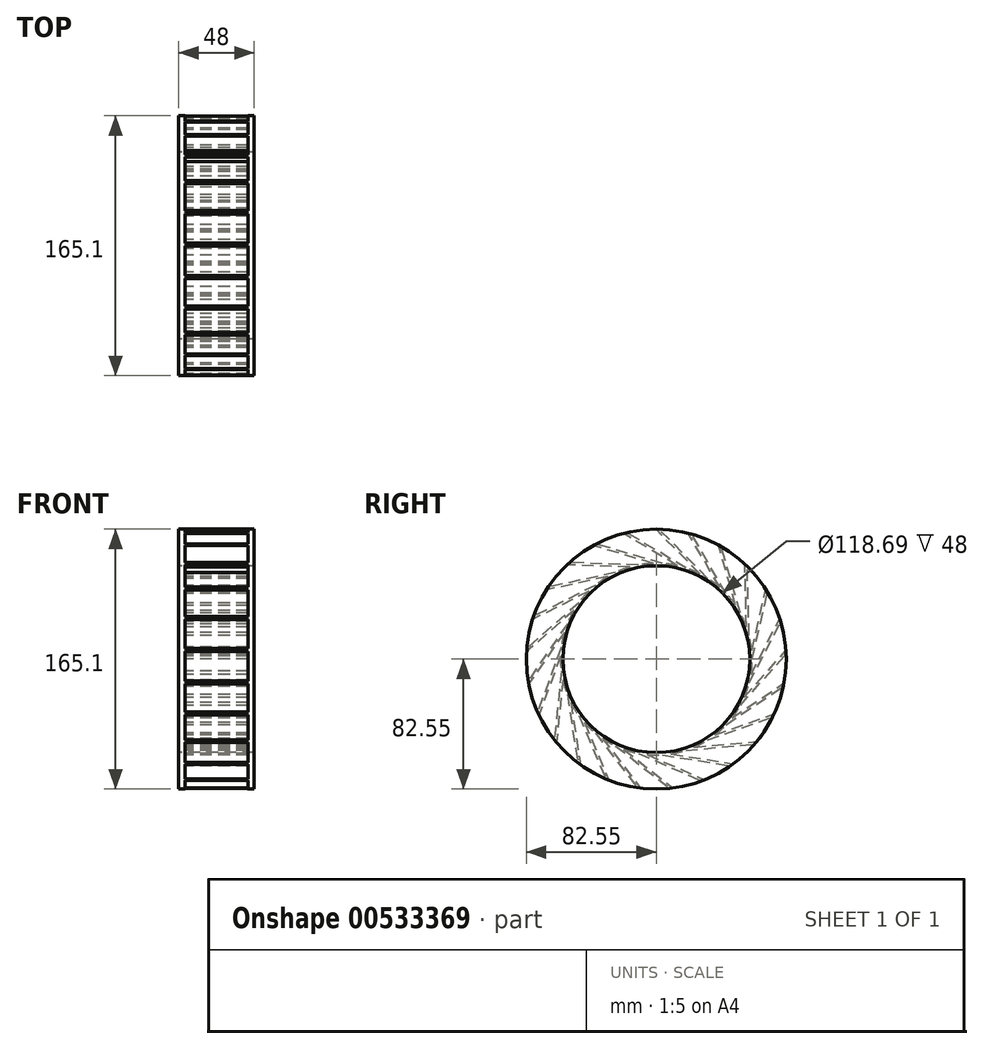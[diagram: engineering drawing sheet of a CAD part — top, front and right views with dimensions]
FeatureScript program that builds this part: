
annotation { "Feature Type Name" : "Feature", "Feature Type Description" : "" }
export const myFeature = defineFeature(function(context is Context, id is Id, definition is map)
    precondition{}
    {
        {
            var Q0;
            Q0=qCreatedBy(makeId("Right.planeOp"),FACE);
            var sketch = newSketch(context, id + "F0", { "sketchPlane" : qUnion([Q0])});
            skCircle(sketch, "E0", {"center": v(0, 0) * mm, "radius": 82.55 * mm});
            skCircle(sketch, "E1", {"center": v(0, 0) * mm, "radius": 60.85 * mm});
            skLineSegment(sketch, "E2", {"start": v(60.85, 0) * mm, "end": v(70.97, 44.2) * mm});
            skLineSegment(sketch, "E3.0", {"start": v(59.38, 0.34) * mm, "end": v(69.5, 44.53) * mm});
            skLineSegment(sketch, "E4", {"start": v(69.5, 44.53) * mm, "end": v(70.97, 44.2) * mm});
            skLineSegment(sketch, "E5.1.0", {"start": v(57.43, 15.1) * mm, "end": v(56.25, 60.42) * mm});
            skLineSegment(sketch, "E5.1.1", {"start": v(58.93, 15.13) * mm, "end": v(57.75, 60.46) * mm});
            skLineSegment(sketch, "E5.2.0", {"start": v(51.88, 28.9) * mm, "end": v(39.46, 72.5) * mm});
            skLineSegment(sketch, "E5.2.1", {"start": v(53.32, 29.31) * mm, "end": v(40.9, 72.92) * mm});
            skLineSegment(sketch, "E5.3.0", {"start": v(43.06, 40.9) * mm, "end": v(20.19, 80.04) * mm});
            skLineSegment(sketch, "E5.3.1", {"start": v(44.35, 41.65) * mm, "end": v(21.48, 80.8) * mm});
            skLineSegment(sketch, "E5.4.0", {"start": v(31.54, 50.32) * mm, "end": v(-0.35, 82.55) * mm});
            skLineSegment(sketch, "E5.4.1", {"start": v(32.6, 51.37) * mm, "end": v(0.71, 83.6) * mm});
            skLineSegment(sketch, "E5.5.0", {"start": v(18.03, 56.58) * mm, "end": v(-20.87, 79.87) * mm});
            skLineSegment(sketch, "E5.5.1", {"start": v(18.8, 57.87) * mm, "end": v(-20.1, 81.15) * mm});
            skLineSegment(sketch, "E5.6.0", {"start": v(3.4, 59.29) * mm, "end": v(-40.08, 72.17) * mm});
            skLineSegment(sketch, "E5.6.1", {"start": v(3.82, 60.73) * mm, "end": v(-39.65, 73.6) * mm});
            skLineSegment(sketch, "E5.7.0", {"start": v(-11.46, 58.27) * mm, "end": v(-56.77, 59.93) * mm});
            skLineSegment(sketch, "E5.7.1", {"start": v(-11.4, 59.77) * mm, "end": v(-56.71, 61.43) * mm});
            skLineSegment(sketch, "E5.8.0", {"start": v(-25.59, 53.59) * mm, "end": v(-69.89, 43.93) * mm});
            skLineSegment(sketch, "E5.8.1", {"start": v(-25.9, 55.05) * mm, "end": v(-70.2, 45.4) * mm});
            skLineSegment(sketch, "E5.9.0", {"start": v(-38.11, 45.54) * mm, "end": v(-78.62, 25.17) * mm});
            skLineSegment(sketch, "E5.9.1", {"start": v(-38.78, 46.88) * mm, "end": v(-79.3, 26.51) * mm});
            skLineSegment(sketch, "E5.10.0", {"start": v(-48.24, 34.63) * mm, "end": v(-82.4, 4.83) * mm});
            skLineSegment(sketch, "E5.10.1", {"start": v(-49.22, 35.76) * mm, "end": v(-83.4, 5.96) * mm});
            skLineSegment(sketch, "E5.11.0", {"start": v(-55.34, 21.55) * mm, "end": v(-81.02, -15.82) * mm});
            skLineSegment(sketch, "E5.11.1", {"start": v(-56.57, 22.4) * mm, "end": v(-82.26, -14.97) * mm});
            skLineSegment(sketch, "E5.12.0", {"start": v(-58.96, 7.11) * mm, "end": v(-74.54, -35.47) * mm});
            skLineSegment(sketch, "E5.12.1", {"start": v(-60.37, 7.63) * mm, "end": v(-75.95, -34.95) * mm});
            skLineSegment(sketch, "E5.13.0", {"start": v(-58.87, -7.78) * mm, "end": v(-63.38, -52.9) * mm});
            skLineSegment(sketch, "E5.13.1", {"start": v(-60.37, -7.63) * mm, "end": v(-64.87, -52.74) * mm});
            skLineSegment(sketch, "E5.14.0", {"start": v(-55.09, -22.17) * mm, "end": v(-48.24, -67) * mm});
            skLineSegment(sketch, "E5.14.1", {"start": v(-56.57, -22.4) * mm, "end": v(-49.72, -67.22) * mm});
            skLineSegment(sketch, "E5.15.0", {"start": v(-47.85, -35.18) * mm, "end": v(-30.06, -76.88) * mm});
            skLineSegment(sketch, "E5.15.1", {"start": v(-49.22, -35.76) * mm, "end": v(-31.44, -77.47) * mm});
            skLineSegment(sketch, "E5.16.0", {"start": v(-37.6, -45.97) * mm, "end": v(-10, -81.94) * mm});
            skLineSegment(sketch, "E5.16.1", {"start": v(-38.78, -46.88) * mm, "end": v(-11.19, -82.86) * mm});
            skLineSegment(sketch, "E5.17.0", {"start": v(-24.98, -53.87) * mm, "end": v(10.7, -81.85) * mm});
            skLineSegment(sketch, "E5.17.1", {"start": v(-25.9, -55.05) * mm, "end": v(9.77, -83.03) * mm});
            skLineSegment(sketch, "E5.18.0", {"start": v(-10.8, -58.4) * mm, "end": v(30.72, -76.62) * mm});
            skLineSegment(sketch, "E5.18.1", {"start": v(-11.4, -59.77) * mm, "end": v(30.11, -78) * mm});
            skLineSegment(sketch, "E5.19.0", {"start": v(4.06, -59.24) * mm, "end": v(48.8, -66.58) * mm});
            skLineSegment(sketch, "E5.19.1", {"start": v(3.82, -60.73) * mm, "end": v(48.56, -68.06) * mm});
            skLineSegment(sketch, "E5.20.0", {"start": v(18.67, -56.37) * mm, "end": v(63.83, -52.35) * mm});
            skLineSegment(sketch, "E5.20.1", {"start": v(18.8, -57.87) * mm, "end": v(63.96, -53.84) * mm});
            skLineSegment(sketch, "E5.21.0", {"start": v(32.1, -49.96) * mm, "end": v(74.84, -34.83) * mm});
            skLineSegment(sketch, "E5.21.1", {"start": v(32.6, -51.37) * mm, "end": v(75.34, -36.24) * mm});
            skLineSegment(sketch, "E5.22.0", {"start": v(43.52, -40.4) * mm, "end": v(81.15, -15.12) * mm});
            skLineSegment(sketch, "E5.22.1", {"start": v(44.35, -41.65) * mm, "end": v(81.99, -16.37) * mm});
            skLineSegment(sketch, "E5.23.0", {"start": v(52.2, -28.31) * mm, "end": v(82.36, 5.54) * mm});
            skLineSegment(sketch, "E5.23.1", {"start": v(53.32, -29.31) * mm, "end": v(83.48, 4.54) * mm});
            skLineSegment(sketch, "E5.24.0", {"start": v(57.6, -14.44) * mm, "end": v(78.4, 25.85) * mm});
            skLineSegment(sketch, "E5.24.1", {"start": v(58.93, -15.13) * mm, "end": v(79.73, 25.16) * mm});
            skLineSegment(sketch, "E6", {"start": v(-60.85, 0) * mm, "end": v(-59.35, 0) * mm});
            skCircle(sketch, "E7", {"center": v(0, 0) * mm, "radius": 59.35 * mm});
            skSolve(sketch);
        }
        {
            var Q0;
            {var subQ0=sQuery(id+"F0.wireOp",EDGE,"E5.22.0");var subQ1=sQuery(id+"F0.wireOp",EDGE,"E0");var subQ2=makeQuery(id+"F0.imprint","INTERSECT",VERTEX,{"derivedFrom":[subQ1,subQ0]});Q0=makeQuery(id+"F0.imprint","IMPRINT",FACE,{"disambiguationData":[TD([[makeQuery(id+"F0.imprint","IMPRINT",EDGE,{"disambiguationData":[TD([[subQ2,-1.0]])],"derivedFrom":subQ1}),1.0]])]});}
            var Q1;
            {var subQ0=sQuery(id+"F0.wireOp",EDGE,"E5.14.0");var subQ1=sQuery(id+"F0.wireOp",EDGE,"E0");var subQ2=makeQuery(id+"F0.imprint","INTERSECT",VERTEX,{"derivedFrom":[subQ1,subQ0]});Q1=makeQuery(id+"F0.imprint","IMPRINT",FACE,{"disambiguationData":[TD([[makeQuery(id+"F0.imprint","IMPRINT",EDGE,{"disambiguationData":[TD([[subQ2,-1.0]])],"derivedFrom":subQ1}),1.0]])]});}
            var Q2;
            {var subQ0=sQuery(id+"F0.wireOp",EDGE,"E5.6.0");var subQ1=sQuery(id+"F0.wireOp",EDGE,"E0");var subQ2=makeQuery(id+"F0.imprint","INTERSECT",VERTEX,{"derivedFrom":[subQ1,subQ0]});Q2=makeQuery(id+"F0.imprint","IMPRINT",FACE,{"disambiguationData":[TD([[makeQuery(id+"F0.imprint","IMPRINT",EDGE,{"disambiguationData":[TD([[subQ2,-1.0]])],"derivedFrom":subQ1}),1.0]])]});}
            var Q3;
            {var subQ0=sQuery(id+"F0.wireOp",EDGE,"E5.9.0");var subQ1=sQuery(id+"F0.wireOp",EDGE,"E0");var subQ2=makeQuery(id+"F0.imprint","INTERSECT",VERTEX,{"derivedFrom":[subQ1,subQ0]});Q3=makeQuery(id+"F0.imprint","IMPRINT",FACE,{"disambiguationData":[TD([[makeQuery(id+"F0.imprint","IMPRINT",EDGE,{"disambiguationData":[TD([[subQ2,-1.0]])],"derivedFrom":subQ1}),1.0]])]});}
            var Q4;
            {var subQ0=sQuery(id+"F0.wireOp",EDGE,"E5.3.0");var subQ1=sQuery(id+"F0.wireOp",EDGE,"E0");var subQ2=makeQuery(id+"F0.imprint","INTERSECT",VERTEX,{"derivedFrom":[subQ1,subQ0]});Q4=makeQuery(id+"F0.imprint","IMPRINT",FACE,{"disambiguationData":[TD([[makeQuery(id+"F0.imprint","IMPRINT",EDGE,{"disambiguationData":[TD([[subQ2,-1.0]])],"derivedFrom":subQ1}),1.0]])]});}
            var Q5;
            {var subQ0=sQuery(id+"F0.wireOp",EDGE,"E5.2.0");var subQ1=sQuery(id+"F0.wireOp",EDGE,"E0");var subQ2=makeQuery(id+"F0.imprint","INTERSECT",VERTEX,{"derivedFrom":[subQ1,subQ0]});Q5=makeQuery(id+"F0.imprint","IMPRINT",FACE,{"disambiguationData":[TD([[makeQuery(id+"F0.imprint","IMPRINT",EDGE,{"disambiguationData":[TD([[subQ2,-1.0]])],"derivedFrom":subQ1}),1.0]])]});}
            var Q6;
            {var subQ0=sQuery(id+"F0.wireOp",EDGE,"E5.1.0");var subQ1=sQuery(id+"F0.wireOp",EDGE,"E0");var subQ2=makeQuery(id+"F0.imprint","INTERSECT",VERTEX,{"derivedFrom":[subQ1,subQ0]});Q6=makeQuery(id+"F0.imprint","IMPRINT",FACE,{"disambiguationData":[TD([[makeQuery(id+"F0.imprint","IMPRINT",EDGE,{"disambiguationData":[TD([[subQ2,-1.0]])],"derivedFrom":subQ1}),1.0]])]});}
            var Q7;
            {var subQ3=sQuery(id+"F0.wireOp",EDGE,"E5.1.1");var subQ5=sQuery(id+"F0.wireOp",EDGE,"E1");var subQ6=makeQuery(id+"F0.imprint","INTERSECT",VERTEX,{"derivedFrom":[subQ5,subQ3]});Q7=makeQuery(id+"F0.imprint","IMPRINT",FACE,{"disambiguationData":[TD([[makeQuery(id+"F0.imprint","IMPRINT",EDGE,{"disambiguationData":[TD([[subQ6,1.0]])],"derivedFrom":subQ5}),-1.0]])]});}
            var Q8;
            {var subQ0=sQuery(id+"F0.wireOp",EDGE,"E5.24.0");var subQ1=sQuery(id+"F0.wireOp",EDGE,"E0");var subQ2=makeQuery(id+"F0.imprint","INTERSECT",VERTEX,{"derivedFrom":[subQ1,subQ0]});Q8=makeQuery(id+"F0.imprint","IMPRINT",FACE,{"disambiguationData":[TD([[makeQuery(id+"F0.imprint","IMPRINT",EDGE,{"disambiguationData":[TD([[subQ2,-1.0]])],"derivedFrom":subQ1}),1.0]])]});}
            var Q9;
            {var subQ0=sQuery(id+"F0.wireOp",EDGE,"E5.21.0");var subQ1=sQuery(id+"F0.wireOp",EDGE,"E0");var subQ2=makeQuery(id+"F0.imprint","INTERSECT",VERTEX,{"derivedFrom":[subQ1,subQ0]});Q9=makeQuery(id+"F0.imprint","IMPRINT",FACE,{"disambiguationData":[TD([[makeQuery(id+"F0.imprint","IMPRINT",EDGE,{"disambiguationData":[TD([[subQ2,-1.0]])],"derivedFrom":subQ1}),1.0]])]});}
            var Q10;
            {var subQ0=sQuery(id+"F0.wireOp",EDGE,"E5.8.0");var subQ1=sQuery(id+"F0.wireOp",EDGE,"E0");var subQ2=makeQuery(id+"F0.imprint","INTERSECT",VERTEX,{"derivedFrom":[subQ1,subQ0]});Q10=makeQuery(id+"F0.imprint","IMPRINT",FACE,{"disambiguationData":[TD([[makeQuery(id+"F0.imprint","IMPRINT",EDGE,{"disambiguationData":[TD([[subQ2,-1.0]])],"derivedFrom":subQ1}),1.0]])]});}
            var Q11;
            {var subQ0=sQuery(id+"F0.wireOp",EDGE,"E5.16.0");var subQ1=sQuery(id+"F0.wireOp",EDGE,"E0");var subQ2=makeQuery(id+"F0.imprint","INTERSECT",VERTEX,{"derivedFrom":[subQ1,subQ0]});Q11=makeQuery(id+"F0.imprint","IMPRINT",FACE,{"disambiguationData":[TD([[makeQuery(id+"F0.imprint","IMPRINT",EDGE,{"disambiguationData":[TD([[subQ2,-1.0]])],"derivedFrom":subQ1}),1.0]])]});}
            var Q12;
            {var subQ0=sQuery(id+"F0.wireOp",EDGE,"E5.11.0");var subQ1=sQuery(id+"F0.wireOp",EDGE,"E0");var subQ2=makeQuery(id+"F0.imprint","INTERSECT",VERTEX,{"derivedFrom":[subQ1,subQ0]});Q12=makeQuery(id+"F0.imprint","IMPRINT",FACE,{"disambiguationData":[TD([[makeQuery(id+"F0.imprint","IMPRINT",EDGE,{"disambiguationData":[TD([[subQ2,-1.0]])],"derivedFrom":subQ1}),1.0]])]});}
            var Q13;
            {var subQ3=sQuery(id+"F0.wireOp",EDGE,"E1");var subQ7=makeQuery(id+"F0.imprint","IMPRINT",VERTEX,{"derivedFrom":subQ3});Q13=makeQuery(id+"F0.imprint","IMPRINT",FACE,{"disambiguationData":[TD([[makeQuery(id+"F0.imprint","IMPRINT",EDGE,{"disambiguationData":[TD([[subQ7,1.0]])],"derivedFrom":subQ3}),-1.0]])]});}
            var Q14;
            {var subQ0=sQuery(id+"F0.wireOp",EDGE,"E5.20.0");var subQ1=sQuery(id+"F0.wireOp",EDGE,"E0");var subQ2=makeQuery(id+"F0.imprint","INTERSECT",VERTEX,{"derivedFrom":[subQ1,subQ0]});Q14=makeQuery(id+"F0.imprint","IMPRINT",FACE,{"disambiguationData":[TD([[makeQuery(id+"F0.imprint","IMPRINT",EDGE,{"disambiguationData":[TD([[subQ2,-1.0]])],"derivedFrom":subQ1}),1.0]])]});}
            var Q15;
            {var subQ0=sQuery(id+"F0.wireOp",EDGE,"E5.15.0");var subQ1=sQuery(id+"F0.wireOp",EDGE,"E0");var subQ2=makeQuery(id+"F0.imprint","INTERSECT",VERTEX,{"derivedFrom":[subQ1,subQ0]});Q15=makeQuery(id+"F0.imprint","IMPRINT",FACE,{"disambiguationData":[TD([[makeQuery(id+"F0.imprint","IMPRINT",EDGE,{"disambiguationData":[TD([[subQ2,-1.0]])],"derivedFrom":subQ1}),1.0]])]});}
            var Q16;
            {var subQ0=sQuery(id+"F0.wireOp",EDGE,"E5.10.0");var subQ1=sQuery(id+"F0.wireOp",EDGE,"E0");var subQ2=makeQuery(id+"F0.imprint","INTERSECT",VERTEX,{"derivedFrom":[subQ1,subQ0]});Q16=makeQuery(id+"F0.imprint","IMPRINT",FACE,{"disambiguationData":[TD([[makeQuery(id+"F0.imprint","IMPRINT",EDGE,{"disambiguationData":[TD([[subQ2,-1.0]])],"derivedFrom":subQ1}),1.0]])]});}
            var Q17;
            {var subQ0=sQuery(id+"F0.wireOp",EDGE,"E5.18.0");var subQ1=sQuery(id+"F0.wireOp",EDGE,"E0");var subQ2=makeQuery(id+"F0.imprint","INTERSECT",VERTEX,{"derivedFrom":[subQ1,subQ0]});Q17=makeQuery(id+"F0.imprint","IMPRINT",FACE,{"disambiguationData":[TD([[makeQuery(id+"F0.imprint","IMPRINT",EDGE,{"disambiguationData":[TD([[subQ2,-1.0]])],"derivedFrom":subQ1}),1.0]])]});}
            var Q18;
            {var subQ0=sQuery(id+"F0.wireOp",EDGE,"E5.17.0");var subQ1=sQuery(id+"F0.wireOp",EDGE,"E0");var subQ2=makeQuery(id+"F0.imprint","INTERSECT",VERTEX,{"derivedFrom":[subQ1,subQ0]});Q18=makeQuery(id+"F0.imprint","IMPRINT",FACE,{"disambiguationData":[TD([[makeQuery(id+"F0.imprint","IMPRINT",EDGE,{"disambiguationData":[TD([[subQ2,-1.0]])],"derivedFrom":subQ1}),1.0]])]});}
            var Q19;
            {var subQ0=sQuery(id+"F0.wireOp",EDGE,"E5.14.0");var subQ1=sQuery(id+"F0.wireOp",EDGE,"E0");var subQ2=makeQuery(id+"F0.imprint","INTERSECT",VERTEX,{"derivedFrom":[subQ1,subQ0]});Q19=makeQuery(id+"F0.imprint","IMPRINT",FACE,{"disambiguationData":[TD([[makeQuery(id+"F0.imprint","IMPRINT",EDGE,{"disambiguationData":[TD([[subQ2,1.0]])],"derivedFrom":subQ1}),1.0]])]});}
            var Q20;
            {var subQ0=sQuery(id+"F0.wireOp",EDGE,"E5.22.0");var subQ1=sQuery(id+"F0.wireOp",EDGE,"E0");var subQ2=makeQuery(id+"F0.imprint","INTERSECT",VERTEX,{"derivedFrom":[subQ1,subQ0]});Q20=makeQuery(id+"F0.imprint","IMPRINT",FACE,{"disambiguationData":[TD([[makeQuery(id+"F0.imprint","IMPRINT",EDGE,{"disambiguationData":[TD([[subQ2,1.0]])],"derivedFrom":subQ1}),1.0]])]});}
            var Q21;
            {var subQ0=sQuery(id+"F0.wireOp",EDGE,"E5.9.0");var subQ1=sQuery(id+"F0.wireOp",EDGE,"E0");var subQ2=makeQuery(id+"F0.imprint","INTERSECT",VERTEX,{"derivedFrom":[subQ1,subQ0]});Q21=makeQuery(id+"F0.imprint","IMPRINT",FACE,{"disambiguationData":[TD([[makeQuery(id+"F0.imprint","IMPRINT",EDGE,{"disambiguationData":[TD([[subQ2,1.0]])],"derivedFrom":subQ1}),1.0]])]});}
            var Q22;
            {var subQ0=sQuery(id+"F0.wireOp",EDGE,"E5.17.0");var subQ1=sQuery(id+"F0.wireOp",EDGE,"E0");var subQ2=makeQuery(id+"F0.imprint","INTERSECT",VERTEX,{"derivedFrom":[subQ1,subQ0]});Q22=makeQuery(id+"F0.imprint","IMPRINT",FACE,{"disambiguationData":[TD([[makeQuery(id+"F0.imprint","IMPRINT",EDGE,{"disambiguationData":[TD([[subQ2,1.0]])],"derivedFrom":subQ1}),1.0]])]});}
            var Q23;
            {var subQ0=sQuery(id+"F0.wireOp",EDGE,"E5.3.0");var subQ1=sQuery(id+"F0.wireOp",EDGE,"E0");var subQ2=makeQuery(id+"F0.imprint","INTERSECT",VERTEX,{"derivedFrom":[subQ1,subQ0]});Q23=makeQuery(id+"F0.imprint","IMPRINT",FACE,{"disambiguationData":[TD([[makeQuery(id+"F0.imprint","IMPRINT",EDGE,{"disambiguationData":[TD([[subQ2,1.0]])],"derivedFrom":subQ1}),1.0]])]});}
            var Q24;
            {var subQ0=sQuery(id+"F0.wireOp",EDGE,"E5.2.0");var subQ1=sQuery(id+"F0.wireOp",EDGE,"E0");var subQ2=makeQuery(id+"F0.imprint","INTERSECT",VERTEX,{"derivedFrom":[subQ1,subQ0]});Q24=makeQuery(id+"F0.imprint","IMPRINT",FACE,{"disambiguationData":[TD([[makeQuery(id+"F0.imprint","IMPRINT",EDGE,{"disambiguationData":[TD([[subQ2,1.0]])],"derivedFrom":subQ1}),1.0]])]});}
            var Q25;
            {var subQ0=sQuery(id+"F0.wireOp",EDGE,"E5.1.0");var subQ1=sQuery(id+"F0.wireOp",EDGE,"E0");var subQ2=makeQuery(id+"F0.imprint","INTERSECT",VERTEX,{"derivedFrom":[subQ1,subQ0]});Q25=makeQuery(id+"F0.imprint","IMPRINT",FACE,{"disambiguationData":[TD([[makeQuery(id+"F0.imprint","IMPRINT",EDGE,{"disambiguationData":[TD([[subQ2,1.0]])],"derivedFrom":subQ1}),1.0]])]});}
            var Q26;
            {var subQ0=sQuery(id+"F0.wireOp",EDGE,"E5.23.0");var subQ1=sQuery(id+"F0.wireOp",EDGE,"E0");var subQ2=makeQuery(id+"F0.imprint","INTERSECT",VERTEX,{"derivedFrom":[subQ1,subQ0]});Q26=makeQuery(id+"F0.imprint","IMPRINT",FACE,{"disambiguationData":[TD([[makeQuery(id+"F0.imprint","IMPRINT",EDGE,{"disambiguationData":[TD([[subQ2,-1.0]])],"derivedFrom":subQ1}),1.0]])]});}
            var Q27;
            {var subQ0=sQuery(id+"F0.wireOp",EDGE,"E5.13.0");var subQ1=sQuery(id+"F0.wireOp",EDGE,"E0");var subQ2=makeQuery(id+"F0.imprint","INTERSECT",VERTEX,{"derivedFrom":[subQ1,subQ0]});Q27=makeQuery(id+"F0.imprint","IMPRINT",FACE,{"disambiguationData":[TD([[makeQuery(id+"F0.imprint","IMPRINT",EDGE,{"disambiguationData":[TD([[subQ2,-1.0]])],"derivedFrom":subQ1}),1.0]])]});}
            var Q28;
            {var subQ0=sQuery(id+"F0.wireOp",EDGE,"E5.5.0");var subQ1=sQuery(id+"F0.wireOp",EDGE,"E0");var subQ2=makeQuery(id+"F0.imprint","INTERSECT",VERTEX,{"derivedFrom":[subQ1,subQ0]});Q28=makeQuery(id+"F0.imprint","IMPRINT",FACE,{"disambiguationData":[TD([[makeQuery(id+"F0.imprint","IMPRINT",EDGE,{"disambiguationData":[TD([[subQ2,-1.0]])],"derivedFrom":subQ1}),1.0]])]});}
            var Q29;
            {var subQ0=sQuery(id+"F0.wireOp",EDGE,"E5.4.0");var subQ1=sQuery(id+"F0.wireOp",EDGE,"E0");var subQ2=makeQuery(id+"F0.imprint","INTERSECT",VERTEX,{"derivedFrom":[subQ1,subQ0]});Q29=makeQuery(id+"F0.imprint","IMPRINT",FACE,{"disambiguationData":[TD([[makeQuery(id+"F0.imprint","IMPRINT",EDGE,{"disambiguationData":[TD([[subQ2,-1.0]])],"derivedFrom":subQ1}),1.0]])]});}
            var Q30;
            {var subQ0=sQuery(id+"F0.wireOp",EDGE,"E5.4.0");var subQ1=sQuery(id+"F0.wireOp",EDGE,"E0");var subQ2=makeQuery(id+"F0.imprint","INTERSECT",VERTEX,{"derivedFrom":[subQ1,subQ0]});Q30=makeQuery(id+"F0.imprint","IMPRINT",FACE,{"disambiguationData":[TD([[makeQuery(id+"F0.imprint","IMPRINT",EDGE,{"disambiguationData":[TD([[subQ2,1.0]])],"derivedFrom":subQ1}),1.0]])]});}
            var Q31;
            {var subQ0=sQuery(id+"F0.wireOp",EDGE,"E5.5.0");var subQ1=sQuery(id+"F0.wireOp",EDGE,"E0");var subQ2=makeQuery(id+"F0.imprint","INTERSECT",VERTEX,{"derivedFrom":[subQ1,subQ0]});Q31=makeQuery(id+"F0.imprint","IMPRINT",FACE,{"disambiguationData":[TD([[makeQuery(id+"F0.imprint","IMPRINT",EDGE,{"disambiguationData":[TD([[subQ2,1.0]])],"derivedFrom":subQ1}),1.0]])]});}
            var Q32;
            {var subQ0=sQuery(id+"F0.wireOp",EDGE,"E5.19.0");var subQ1=sQuery(id+"F0.wireOp",EDGE,"E0");var subQ2=makeQuery(id+"F0.imprint","INTERSECT",VERTEX,{"derivedFrom":[subQ1,subQ0]});Q32=makeQuery(id+"F0.imprint","IMPRINT",FACE,{"disambiguationData":[TD([[makeQuery(id+"F0.imprint","IMPRINT",EDGE,{"disambiguationData":[TD([[subQ2,-1.0]])],"derivedFrom":subQ1}),1.0]])]});}
            var Q33;
            {var subQ0=sQuery(id+"F0.wireOp",EDGE,"E5.8.0");var subQ1=sQuery(id+"F0.wireOp",EDGE,"E0");var subQ2=makeQuery(id+"F0.imprint","INTERSECT",VERTEX,{"derivedFrom":[subQ1,subQ0]});Q33=makeQuery(id+"F0.imprint","IMPRINT",FACE,{"disambiguationData":[TD([[makeQuery(id+"F0.imprint","IMPRINT",EDGE,{"disambiguationData":[TD([[subQ2,1.0]])],"derivedFrom":subQ1}),1.0]])]});}
            var Q34;
            {var subQ0=sQuery(id+"F0.wireOp",EDGE,"E5.11.0");var subQ1=sQuery(id+"F0.wireOp",EDGE,"E0");var subQ2=makeQuery(id+"F0.imprint","INTERSECT",VERTEX,{"derivedFrom":[subQ1,subQ0]});Q34=makeQuery(id+"F0.imprint","IMPRINT",FACE,{"disambiguationData":[TD([[makeQuery(id+"F0.imprint","IMPRINT",EDGE,{"disambiguationData":[TD([[subQ2,1.0]])],"derivedFrom":subQ1}),1.0]])]});}
            var Q35;
            {var subQ0=sQuery(id+"F0.wireOp",EDGE,"E5.19.0");var subQ1=sQuery(id+"F0.wireOp",EDGE,"E0");var subQ2=makeQuery(id+"F0.imprint","INTERSECT",VERTEX,{"derivedFrom":[subQ1,subQ0]});Q35=makeQuery(id+"F0.imprint","IMPRINT",FACE,{"disambiguationData":[TD([[makeQuery(id+"F0.imprint","IMPRINT",EDGE,{"disambiguationData":[TD([[subQ2,1.0]])],"derivedFrom":subQ1}),1.0]])]});}
            var Q36;
            {var subQ0=sQuery(id+"F0.wireOp",EDGE,"E5.12.0");var subQ1=sQuery(id+"F0.wireOp",EDGE,"E0");var subQ2=makeQuery(id+"F0.imprint","INTERSECT",VERTEX,{"derivedFrom":[subQ1,subQ0]});Q36=makeQuery(id+"F0.imprint","IMPRINT",FACE,{"disambiguationData":[TD([[makeQuery(id+"F0.imprint","IMPRINT",EDGE,{"disambiguationData":[TD([[subQ2,1.0]])],"derivedFrom":subQ1}),1.0]])]});}
            var Q37;
            {var subQ0=sQuery(id+"F0.wireOp",EDGE,"E5.7.0");var subQ1=sQuery(id+"F0.wireOp",EDGE,"E0");var subQ2=makeQuery(id+"F0.imprint","INTERSECT",VERTEX,{"derivedFrom":[subQ1,subQ0]});Q37=makeQuery(id+"F0.imprint","IMPRINT",FACE,{"disambiguationData":[TD([[makeQuery(id+"F0.imprint","IMPRINT",EDGE,{"disambiguationData":[TD([[subQ2,-1.0]])],"derivedFrom":subQ1}),1.0]])]});}
            var Q38;
            {var subQ0=sQuery(id+"F0.wireOp",EDGE,"E5.15.0");var subQ1=sQuery(id+"F0.wireOp",EDGE,"E0");var subQ2=makeQuery(id+"F0.imprint","INTERSECT",VERTEX,{"derivedFrom":[subQ1,subQ0]});Q38=makeQuery(id+"F0.imprint","IMPRINT",FACE,{"disambiguationData":[TD([[makeQuery(id+"F0.imprint","IMPRINT",EDGE,{"disambiguationData":[TD([[subQ2,1.0]])],"derivedFrom":subQ1}),1.0]])]});}
            var Q39;
            {var subQ3=sQuery(id+"F0.wireOp",EDGE,"E2");var subQ5=sQuery(id+"F0.wireOp",EDGE,"E1");var subQ6=makeQuery(id+"F0.imprint","INTERSECT",VERTEX,{"derivedFrom":[subQ5,subQ3]});Q39=makeQuery(id+"F0.imprint","IMPRINT",FACE,{"disambiguationData":[TD([[makeQuery(id+"F0.imprint","IMPRINT",EDGE,{"disambiguationData":[TD([[subQ6,-1.0]])],"derivedFrom":subQ5}),-1.0]])]});}
            var Q40;
            {var subQ0=sQuery(id+"F0.wireOp",EDGE,"E5.21.0");var subQ1=sQuery(id+"F0.wireOp",EDGE,"E0");var subQ2=makeQuery(id+"F0.imprint","INTERSECT",VERTEX,{"derivedFrom":[subQ1,subQ0]});Q40=makeQuery(id+"F0.imprint","IMPRINT",FACE,{"disambiguationData":[TD([[makeQuery(id+"F0.imprint","IMPRINT",EDGE,{"disambiguationData":[TD([[subQ2,1.0]])],"derivedFrom":subQ1}),1.0]])]});}
            var Q41;
            {var subQ0=sQuery(id+"F0.wireOp",EDGE,"E5.13.0");var subQ1=sQuery(id+"F0.wireOp",EDGE,"E0");var subQ2=makeQuery(id+"F0.imprint","INTERSECT",VERTEX,{"derivedFrom":[subQ1,subQ0]});Q41=makeQuery(id+"F0.imprint","IMPRINT",FACE,{"disambiguationData":[TD([[makeQuery(id+"F0.imprint","IMPRINT",EDGE,{"disambiguationData":[TD([[subQ2,1.0]])],"derivedFrom":subQ1}),1.0]])]});}
            var Q42;
            {var subQ0=sQuery(id+"F0.wireOp",EDGE,"E5.18.0");var subQ1=sQuery(id+"F0.wireOp",EDGE,"E0");var subQ2=makeQuery(id+"F0.imprint","INTERSECT",VERTEX,{"derivedFrom":[subQ1,subQ0]});Q42=makeQuery(id+"F0.imprint","IMPRINT",FACE,{"disambiguationData":[TD([[makeQuery(id+"F0.imprint","IMPRINT",EDGE,{"disambiguationData":[TD([[subQ2,1.0]])],"derivedFrom":subQ1}),1.0]])]});}
            var Q43;
            {var subQ0=sQuery(id+"F0.wireOp",EDGE,"E5.10.0");var subQ1=sQuery(id+"F0.wireOp",EDGE,"E0");var subQ2=makeQuery(id+"F0.imprint","INTERSECT",VERTEX,{"derivedFrom":[subQ1,subQ0]});Q43=makeQuery(id+"F0.imprint","IMPRINT",FACE,{"disambiguationData":[TD([[makeQuery(id+"F0.imprint","IMPRINT",EDGE,{"disambiguationData":[TD([[subQ2,1.0]])],"derivedFrom":subQ1}),1.0]])]});}
            var Q44;
            {var subQ0=sQuery(id+"F0.wireOp",EDGE,"E5.6.0");var subQ1=sQuery(id+"F0.wireOp",EDGE,"E0");var subQ2=makeQuery(id+"F0.imprint","INTERSECT",VERTEX,{"derivedFrom":[subQ1,subQ0]});Q44=makeQuery(id+"F0.imprint","IMPRINT",FACE,{"disambiguationData":[TD([[makeQuery(id+"F0.imprint","IMPRINT",EDGE,{"disambiguationData":[TD([[subQ2,1.0]])],"derivedFrom":subQ1}),1.0]])]});}
            var Q45;
            {var subQ0=sQuery(id+"F0.wireOp",EDGE,"E5.24.0");var subQ1=sQuery(id+"F0.wireOp",EDGE,"E0");var subQ2=makeQuery(id+"F0.imprint","INTERSECT",VERTEX,{"derivedFrom":[subQ1,subQ0]});Q45=makeQuery(id+"F0.imprint","IMPRINT",FACE,{"disambiguationData":[TD([[makeQuery(id+"F0.imprint","IMPRINT",EDGE,{"disambiguationData":[TD([[subQ2,1.0]])],"derivedFrom":subQ1}),1.0]])]});}
            var Q46;
            {var subQ0=sQuery(id+"F0.wireOp",EDGE,"E5.23.0");var subQ1=sQuery(id+"F0.wireOp",EDGE,"E0");var subQ2=makeQuery(id+"F0.imprint","INTERSECT",VERTEX,{"derivedFrom":[subQ1,subQ0]});Q46=makeQuery(id+"F0.imprint","IMPRINT",FACE,{"disambiguationData":[TD([[makeQuery(id+"F0.imprint","IMPRINT",EDGE,{"disambiguationData":[TD([[subQ2,1.0]])],"derivedFrom":subQ1}),1.0]])]});}
            var Q47;
            {var subQ0=sQuery(id+"F0.wireOp",EDGE,"E5.16.0");var subQ1=sQuery(id+"F0.wireOp",EDGE,"E0");var subQ2=makeQuery(id+"F0.imprint","INTERSECT",VERTEX,{"derivedFrom":[subQ1,subQ0]});Q47=makeQuery(id+"F0.imprint","IMPRINT",FACE,{"disambiguationData":[TD([[makeQuery(id+"F0.imprint","IMPRINT",EDGE,{"disambiguationData":[TD([[subQ2,1.0]])],"derivedFrom":subQ1}),1.0]])]});}
            var Q48;
            Q48=makeQuery(id+"F0.imprint","IMPRINT",FACE,{"disambiguationData":[TD([[makeQuery(id+"F0.imprint","IMPRINT",EDGE,{"derivedFrom":sQuery(id+"F0.wireOp",EDGE,"E7")}),-1.0]])]});
            var Q49;
            {var subQ0=sQuery(id+"F0.wireOp",EDGE,"E5.20.0");var subQ1=sQuery(id+"F0.wireOp",EDGE,"E0");var subQ2=makeQuery(id+"F0.imprint","INTERSECT",VERTEX,{"derivedFrom":[subQ1,subQ0]});Q49=makeQuery(id+"F0.imprint","IMPRINT",FACE,{"disambiguationData":[TD([[makeQuery(id+"F0.imprint","IMPRINT",EDGE,{"disambiguationData":[TD([[subQ2,1.0]])],"derivedFrom":subQ1}),1.0]])]});}
            var Q50;
            {var subQ0=sQuery(id+"F0.wireOp",EDGE,"E5.7.0");var subQ1=sQuery(id+"F0.wireOp",EDGE,"E0");var subQ2=makeQuery(id+"F0.imprint","INTERSECT",VERTEX,{"derivedFrom":[subQ1,subQ0]});Q50=makeQuery(id+"F0.imprint","IMPRINT",FACE,{"disambiguationData":[TD([[makeQuery(id+"F0.imprint","IMPRINT",EDGE,{"disambiguationData":[TD([[subQ2,1.0]])],"derivedFrom":subQ1}),1.0]])]});}
            extrude(context, id + "F1", {"entities" : qUnion([Q0, Q1, Q2, Q3, Q4, Q5, Q6, Q7, Q8, Q9, Q10, Q11, Q12, Q13, Q14, Q15, Q16, Q17, Q18, Q19, Q20, Q21, Q22, Q23, Q24, Q25, Q26, Q27, Q28, Q29, Q30, Q31, Q32, Q33, Q34, Q35, Q36, Q37, Q38, Q39, Q40, Q41, Q42, Q43, Q44, Q45, Q46, Q47, Q48, Q49, Q50]), "depth" : 44 * mm, "offsetDistance" : 25 * mm, "hasSecondDirection" : true, "secondDirectionOppositeDirection" : true, "secondDirectionDepth" : 4 * mm});
        }
        {
            var Q0;
            {var subQ3=sQuery(id+"F0.wireOp",EDGE,"E5.1.1");var subQ5=sQuery(id+"F0.wireOp",EDGE,"E1");var subQ6=makeQuery(id+"F0.imprint","INTERSECT",VERTEX,{"derivedFrom":[subQ5,subQ3]});Q0=makeQuery(id+"F0.imprint","IMPRINT",FACE,{"disambiguationData":[TD([[makeQuery(id+"F0.imprint","IMPRINT",EDGE,{"disambiguationData":[TD([[subQ6,1.0]])],"derivedFrom":subQ5}),-1.0]])]});}
            var Q1;
            {var subQ0=sQuery(id+"F0.wireOp",EDGE,"E5.1.0");var subQ1=sQuery(id+"F0.wireOp",EDGE,"E0");var subQ2=makeQuery(id+"F0.imprint","INTERSECT",VERTEX,{"derivedFrom":[subQ1,subQ0]});Q1=makeQuery(id+"F0.imprint","IMPRINT",FACE,{"disambiguationData":[TD([[makeQuery(id+"F0.imprint","IMPRINT",EDGE,{"disambiguationData":[TD([[subQ2,-1.0]])],"derivedFrom":subQ1}),1.0]])]});}
            var Q2;
            {var subQ0=sQuery(id+"F0.wireOp",EDGE,"E5.2.0");var subQ1=sQuery(id+"F0.wireOp",EDGE,"E0");var subQ2=makeQuery(id+"F0.imprint","INTERSECT",VERTEX,{"derivedFrom":[subQ1,subQ0]});Q2=makeQuery(id+"F0.imprint","IMPRINT",FACE,{"disambiguationData":[TD([[makeQuery(id+"F0.imprint","IMPRINT",EDGE,{"disambiguationData":[TD([[subQ2,-1.0]])],"derivedFrom":subQ1}),1.0]])]});}
            var Q3;
            {var subQ0=sQuery(id+"F0.wireOp",EDGE,"E5.3.0");var subQ1=sQuery(id+"F0.wireOp",EDGE,"E0");var subQ2=makeQuery(id+"F0.imprint","INTERSECT",VERTEX,{"derivedFrom":[subQ1,subQ0]});Q3=makeQuery(id+"F0.imprint","IMPRINT",FACE,{"disambiguationData":[TD([[makeQuery(id+"F0.imprint","IMPRINT",EDGE,{"disambiguationData":[TD([[subQ2,-1.0]])],"derivedFrom":subQ1}),1.0]])]});}
            var Q4;
            {var subQ0=sQuery(id+"F0.wireOp",EDGE,"E5.24.0");var subQ1=sQuery(id+"F0.wireOp",EDGE,"E0");var subQ2=makeQuery(id+"F0.imprint","INTERSECT",VERTEX,{"derivedFrom":[subQ1,subQ0]});Q4=makeQuery(id+"F0.imprint","IMPRINT",FACE,{"disambiguationData":[TD([[makeQuery(id+"F0.imprint","IMPRINT",EDGE,{"disambiguationData":[TD([[subQ2,-1.0]])],"derivedFrom":subQ1}),1.0]])]});}
            var Q5;
            {var subQ0=sQuery(id+"F0.wireOp",EDGE,"E5.23.0");var subQ1=sQuery(id+"F0.wireOp",EDGE,"E0");var subQ2=makeQuery(id+"F0.imprint","INTERSECT",VERTEX,{"derivedFrom":[subQ1,subQ0]});Q5=makeQuery(id+"F0.imprint","IMPRINT",FACE,{"disambiguationData":[TD([[makeQuery(id+"F0.imprint","IMPRINT",EDGE,{"disambiguationData":[TD([[subQ2,-1.0]])],"derivedFrom":subQ1}),1.0]])]});}
            var Q6;
            {var subQ0=sQuery(id+"F0.wireOp",EDGE,"E5.22.0");var subQ1=sQuery(id+"F0.wireOp",EDGE,"E0");var subQ2=makeQuery(id+"F0.imprint","INTERSECT",VERTEX,{"derivedFrom":[subQ1,subQ0]});Q6=makeQuery(id+"F0.imprint","IMPRINT",FACE,{"disambiguationData":[TD([[makeQuery(id+"F0.imprint","IMPRINT",EDGE,{"disambiguationData":[TD([[subQ2,-1.0]])],"derivedFrom":subQ1}),1.0]])]});}
            var Q7;
            {var subQ0=sQuery(id+"F0.wireOp",EDGE,"E5.21.0");var subQ1=sQuery(id+"F0.wireOp",EDGE,"E0");var subQ2=makeQuery(id+"F0.imprint","INTERSECT",VERTEX,{"derivedFrom":[subQ1,subQ0]});Q7=makeQuery(id+"F0.imprint","IMPRINT",FACE,{"disambiguationData":[TD([[makeQuery(id+"F0.imprint","IMPRINT",EDGE,{"disambiguationData":[TD([[subQ2,-1.0]])],"derivedFrom":subQ1}),1.0]])]});}
            var Q8;
            {var subQ0=sQuery(id+"F0.wireOp",EDGE,"E5.20.0");var subQ1=sQuery(id+"F0.wireOp",EDGE,"E0");var subQ2=makeQuery(id+"F0.imprint","INTERSECT",VERTEX,{"derivedFrom":[subQ1,subQ0]});Q8=makeQuery(id+"F0.imprint","IMPRINT",FACE,{"disambiguationData":[TD([[makeQuery(id+"F0.imprint","IMPRINT",EDGE,{"disambiguationData":[TD([[subQ2,-1.0]])],"derivedFrom":subQ1}),1.0]])]});}
            var Q9;
            {var subQ0=sQuery(id+"F0.wireOp",EDGE,"E5.19.0");var subQ1=sQuery(id+"F0.wireOp",EDGE,"E0");var subQ2=makeQuery(id+"F0.imprint","INTERSECT",VERTEX,{"derivedFrom":[subQ1,subQ0]});Q9=makeQuery(id+"F0.imprint","IMPRINT",FACE,{"disambiguationData":[TD([[makeQuery(id+"F0.imprint","IMPRINT",EDGE,{"disambiguationData":[TD([[subQ2,-1.0]])],"derivedFrom":subQ1}),1.0]])]});}
            var Q10;
            {var subQ0=sQuery(id+"F0.wireOp",EDGE,"E5.18.0");var subQ1=sQuery(id+"F0.wireOp",EDGE,"E0");var subQ2=makeQuery(id+"F0.imprint","INTERSECT",VERTEX,{"derivedFrom":[subQ1,subQ0]});Q10=makeQuery(id+"F0.imprint","IMPRINT",FACE,{"disambiguationData":[TD([[makeQuery(id+"F0.imprint","IMPRINT",EDGE,{"disambiguationData":[TD([[subQ2,-1.0]])],"derivedFrom":subQ1}),1.0]])]});}
            var Q11;
            {var subQ0=sQuery(id+"F0.wireOp",EDGE,"E5.17.0");var subQ1=sQuery(id+"F0.wireOp",EDGE,"E0");var subQ2=makeQuery(id+"F0.imprint","INTERSECT",VERTEX,{"derivedFrom":[subQ1,subQ0]});Q11=makeQuery(id+"F0.imprint","IMPRINT",FACE,{"disambiguationData":[TD([[makeQuery(id+"F0.imprint","IMPRINT",EDGE,{"disambiguationData":[TD([[subQ2,-1.0]])],"derivedFrom":subQ1}),1.0]])]});}
            var Q12;
            {var subQ0=sQuery(id+"F0.wireOp",EDGE,"E5.16.0");var subQ1=sQuery(id+"F0.wireOp",EDGE,"E0");var subQ2=makeQuery(id+"F0.imprint","INTERSECT",VERTEX,{"derivedFrom":[subQ1,subQ0]});Q12=makeQuery(id+"F0.imprint","IMPRINT",FACE,{"disambiguationData":[TD([[makeQuery(id+"F0.imprint","IMPRINT",EDGE,{"disambiguationData":[TD([[subQ2,-1.0]])],"derivedFrom":subQ1}),1.0]])]});}
            var Q13;
            {var subQ0=sQuery(id+"F0.wireOp",EDGE,"E5.15.0");var subQ1=sQuery(id+"F0.wireOp",EDGE,"E0");var subQ2=makeQuery(id+"F0.imprint","INTERSECT",VERTEX,{"derivedFrom":[subQ1,subQ0]});Q13=makeQuery(id+"F0.imprint","IMPRINT",FACE,{"disambiguationData":[TD([[makeQuery(id+"F0.imprint","IMPRINT",EDGE,{"disambiguationData":[TD([[subQ2,-1.0]])],"derivedFrom":subQ1}),1.0]])]});}
            var Q14;
            {var subQ0=sQuery(id+"F0.wireOp",EDGE,"E5.14.0");var subQ1=sQuery(id+"F0.wireOp",EDGE,"E0");var subQ2=makeQuery(id+"F0.imprint","INTERSECT",VERTEX,{"derivedFrom":[subQ1,subQ0]});Q14=makeQuery(id+"F0.imprint","IMPRINT",FACE,{"disambiguationData":[TD([[makeQuery(id+"F0.imprint","IMPRINT",EDGE,{"disambiguationData":[TD([[subQ2,-1.0]])],"derivedFrom":subQ1}),1.0]])]});}
            var Q15;
            {var subQ0=sQuery(id+"F0.wireOp",EDGE,"E5.13.0");var subQ1=sQuery(id+"F0.wireOp",EDGE,"E0");var subQ2=makeQuery(id+"F0.imprint","INTERSECT",VERTEX,{"derivedFrom":[subQ1,subQ0]});Q15=makeQuery(id+"F0.imprint","IMPRINT",FACE,{"disambiguationData":[TD([[makeQuery(id+"F0.imprint","IMPRINT",EDGE,{"disambiguationData":[TD([[subQ2,-1.0]])],"derivedFrom":subQ1}),1.0]])]});}
            var Q16;
            {var subQ3=sQuery(id+"F0.wireOp",EDGE,"E1");var subQ7=makeQuery(id+"F0.imprint","IMPRINT",VERTEX,{"derivedFrom":subQ3});Q16=makeQuery(id+"F0.imprint","IMPRINT",FACE,{"disambiguationData":[TD([[makeQuery(id+"F0.imprint","IMPRINT",EDGE,{"disambiguationData":[TD([[subQ7,1.0]])],"derivedFrom":subQ3}),-1.0]])]});}
            var Q17;
            {var subQ0=sQuery(id+"F0.wireOp",EDGE,"E5.11.0");var subQ1=sQuery(id+"F0.wireOp",EDGE,"E0");var subQ2=makeQuery(id+"F0.imprint","INTERSECT",VERTEX,{"derivedFrom":[subQ1,subQ0]});Q17=makeQuery(id+"F0.imprint","IMPRINT",FACE,{"disambiguationData":[TD([[makeQuery(id+"F0.imprint","IMPRINT",EDGE,{"disambiguationData":[TD([[subQ2,-1.0]])],"derivedFrom":subQ1}),1.0]])]});}
            var Q18;
            {var subQ0=sQuery(id+"F0.wireOp",EDGE,"E5.10.0");var subQ1=sQuery(id+"F0.wireOp",EDGE,"E0");var subQ2=makeQuery(id+"F0.imprint","INTERSECT",VERTEX,{"derivedFrom":[subQ1,subQ0]});Q18=makeQuery(id+"F0.imprint","IMPRINT",FACE,{"disambiguationData":[TD([[makeQuery(id+"F0.imprint","IMPRINT",EDGE,{"disambiguationData":[TD([[subQ2,-1.0]])],"derivedFrom":subQ1}),1.0]])]});}
            var Q19;
            {var subQ0=sQuery(id+"F0.wireOp",EDGE,"E5.9.0");var subQ1=sQuery(id+"F0.wireOp",EDGE,"E0");var subQ2=makeQuery(id+"F0.imprint","INTERSECT",VERTEX,{"derivedFrom":[subQ1,subQ0]});Q19=makeQuery(id+"F0.imprint","IMPRINT",FACE,{"disambiguationData":[TD([[makeQuery(id+"F0.imprint","IMPRINT",EDGE,{"disambiguationData":[TD([[subQ2,-1.0]])],"derivedFrom":subQ1}),1.0]])]});}
            var Q20;
            {var subQ0=sQuery(id+"F0.wireOp",EDGE,"E5.8.0");var subQ1=sQuery(id+"F0.wireOp",EDGE,"E0");var subQ2=makeQuery(id+"F0.imprint","INTERSECT",VERTEX,{"derivedFrom":[subQ1,subQ0]});Q20=makeQuery(id+"F0.imprint","IMPRINT",FACE,{"disambiguationData":[TD([[makeQuery(id+"F0.imprint","IMPRINT",EDGE,{"disambiguationData":[TD([[subQ2,-1.0]])],"derivedFrom":subQ1}),1.0]])]});}
            var Q21;
            {var subQ0=sQuery(id+"F0.wireOp",EDGE,"E5.7.0");var subQ1=sQuery(id+"F0.wireOp",EDGE,"E0");var subQ2=makeQuery(id+"F0.imprint","INTERSECT",VERTEX,{"derivedFrom":[subQ1,subQ0]});Q21=makeQuery(id+"F0.imprint","IMPRINT",FACE,{"disambiguationData":[TD([[makeQuery(id+"F0.imprint","IMPRINT",EDGE,{"disambiguationData":[TD([[subQ2,-1.0]])],"derivedFrom":subQ1}),1.0]])]});}
            var Q22;
            {var subQ0=sQuery(id+"F0.wireOp",EDGE,"E5.6.0");var subQ1=sQuery(id+"F0.wireOp",EDGE,"E0");var subQ2=makeQuery(id+"F0.imprint","INTERSECT",VERTEX,{"derivedFrom":[subQ1,subQ0]});Q22=makeQuery(id+"F0.imprint","IMPRINT",FACE,{"disambiguationData":[TD([[makeQuery(id+"F0.imprint","IMPRINT",EDGE,{"disambiguationData":[TD([[subQ2,-1.0]])],"derivedFrom":subQ1}),1.0]])]});}
            var Q23;
            {var subQ0=sQuery(id+"F0.wireOp",EDGE,"E5.5.0");var subQ1=sQuery(id+"F0.wireOp",EDGE,"E0");var subQ2=makeQuery(id+"F0.imprint","INTERSECT",VERTEX,{"derivedFrom":[subQ1,subQ0]});Q23=makeQuery(id+"F0.imprint","IMPRINT",FACE,{"disambiguationData":[TD([[makeQuery(id+"F0.imprint","IMPRINT",EDGE,{"disambiguationData":[TD([[subQ2,-1.0]])],"derivedFrom":subQ1}),1.0]])]});}
            var Q24;
            {var subQ0=sQuery(id+"F0.wireOp",EDGE,"E5.4.0");var subQ1=sQuery(id+"F0.wireOp",EDGE,"E0");var subQ2=makeQuery(id+"F0.imprint","INTERSECT",VERTEX,{"derivedFrom":[subQ1,subQ0]});Q24=makeQuery(id+"F0.imprint","IMPRINT",FACE,{"disambiguationData":[TD([[makeQuery(id+"F0.imprint","IMPRINT",EDGE,{"disambiguationData":[TD([[subQ2,-1.0]])],"derivedFrom":subQ1}),1.0]])]});}
            extrude(context, id + "F2", {"entities" : qUnion([Q0, Q1, Q2, Q3, Q4, Q5, Q6, Q7, Q8, Q9, Q10, Q11, Q12, Q13, Q14, Q15, Q16, Q17, Q18, Q19, Q20, Q21, Q22, Q23, Q24]), "operationType" : NewBodyOperationType.REMOVE, "depth" : 40 * mm, "offsetDistance" : 25 * mm});
        }
    });
